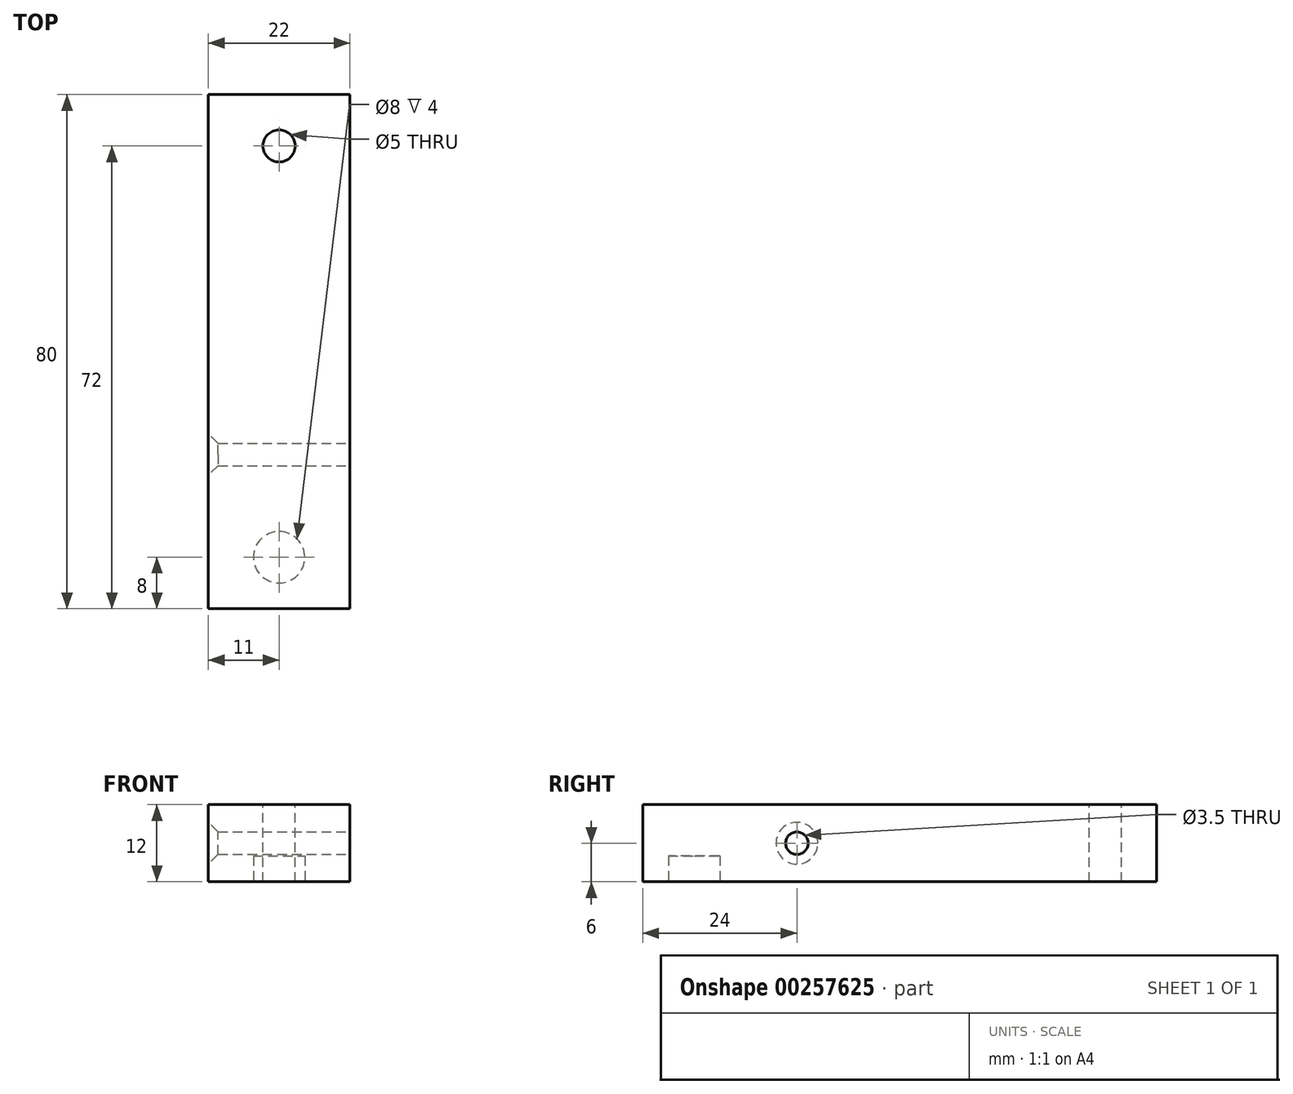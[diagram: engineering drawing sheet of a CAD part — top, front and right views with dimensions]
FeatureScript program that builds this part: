
annotation { "Feature Type Name" : "Feature", "Feature Type Description" : "" }
export const myFeature = defineFeature(function(context is Context, id is Id, definition is map)
    precondition{}
    {
        {
            var Q0;
            Q0=qCreatedBy(makeId("Top.planeOp"),FACE);
            var sketch = newSketch(context, id + "F0", { "sketchPlane" : qUnion([Q0])});
            skLineSegment(sketch, "E0.bottom", {"start": v(11, -40) * mm, "end": v(-11, -40) * mm});
            skLineSegment(sketch, "E0.top", {"start": v(11, 40) * mm, "end": v(-11, 40) * mm});
            skLineSegment(sketch, "E0.left", {"start": v(11, -40) * mm, "end": v(11, 40) * mm});
            skLineSegment(sketch, "E0.right", {"start": v(-11, -40) * mm, "end": v(-11, 40) * mm});
            skPoint(sketch, "E0.middle", {"position": v(0, 0) * mm});
            skSolve(sketch);
        }
        {
            var Q0;
            Q0 = qSketchRegion(id + "F0", true);
            extrude(context, id + "F1", {"entities" : qUnion([Q0]), "depth" : 12 * mm});
        }
        {
            var Q0;
            Q0=makeQuery(id+"F1.opExtrude","SWEPT_FACE",FACE,{"disambiguationData":[OSD([sQuery(id+"F0.wireOp",EDGE,"E0.left")])]});
            var sketch = newSketch(context, id + "F2", { "sketchPlane" : qUnion([Q0])});
            skCircle(sketch, "E1", {"center": v(-16, 6) * mm, "radius": 1.75 * mm});
            skSolve(sketch);
        }
        {
            var Q0;
            Q0 = qSketchRegion(id + "F2", true);
            extrude(context, id + "F3", {"entities" : qUnion([Q0]), "operationType" : NewBodyOperationType.REMOVE, "oppositeDirection" : true, "depth" : 25 * mm});
        }
        {
            var Q0;
            Q0=makeQuery(id+"F3.boolean.opBoolean","COPY",EDGE,{"derivedFrom":makeQuery(id+"F3.opExtrude","CAP_EDGE",EDGE,{"disambiguationData":[OSD([sQuery(id+"F2.wireOp",EDGE,"E1")])],"isStart":true})});
            var Q1;
            Q1=makeQuery(id+"F3.boolean.opBoolean","INTERSECT",EDGE,{"derivedFrom":[makeQuery(id+"F1.opExtrude","SWEPT_FACE",FACE,{"disambiguationData":[OSD([sQuery(id+"F0.wireOp",EDGE,"E0.right")])]}),makeQuery(id+"F3.opExtrude","SWEPT_FACE",FACE,{"disambiguationData":[OSD([sQuery(id+"F2.wireOp",EDGE,"E1")])]})]});
            chamfer(context, id + "F4", {"entities" : qUnion([Q0, Q1]), "width" : 1.5 * mm, "tangentPropagation" : true});
        }
        {
            var Q0;
            Q0=makeQuery(id+"F1.opExtrude","CAP_FACE",FACE,{"disambiguationData":[OSD([sQuery(id+"F0.wireOp",EDGE,"E0.bottom"),sQuery(id+"F0.wireOp",EDGE,"E0.top"),sQuery(id+"F0.wireOp",EDGE,"E0.left"),sQuery(id+"F0.wireOp",EDGE,"E0.right")])],"isStart":true});
            var sketch = newSketch(context, id + "F5", { "sketchPlane" : qUnion([Q0])});
            skCircle(sketch, "E2", {"center": v(0, 32) * mm, "radius": 4 * mm});
            skSolve(sketch);
        }
        {
            var Q0;
            Q0 = qSketchRegion(id + "F5", true);
            extrude(context, id + "F6", {"entities" : qUnion([Q0]), "operationType" : NewBodyOperationType.REMOVE, "oppositeDirection" : true, "depth" : 4 * mm});
        }
        {
            var Q0;
            Q0=makeQuery(id+"F1.opExtrude","CAP_FACE",FACE,{"disambiguationData":[OSD([sQuery(id+"F0.wireOp",EDGE,"E0.bottom"),sQuery(id+"F0.wireOp",EDGE,"E0.top"),sQuery(id+"F0.wireOp",EDGE,"E0.left"),sQuery(id+"F0.wireOp",EDGE,"E0.right")])],"isStart":false});
            var sketch = newSketch(context, id + "F7", { "sketchPlane" : qUnion([Q0])});
            skPoint(sketch, "E3", {"position": v(0, 32) * mm});
            skSolve(sketch);
        }
        {
            var Q0;
            Q0=sQuery(id+"F7.wireOp",VERTEX,"E3");
            var Q1;
            Q1=makeQuery(id+"F1.opExtrude","SWEPT_BODY",BODY,{"disambiguationData":[OSD([sQuery(id+"F0.wireOp",EDGE,"E0.bottom"),sQuery(id+"F0.wireOp",EDGE,"E0.top"),sQuery(id+"F0.wireOp",EDGE,"E0.left"),sQuery(id+"F0.wireOp",EDGE,"E0.right")])]});
            hole(context, id + "F8", {"style" : HoleStyle.SIMPLE, "endStyle" : HoleEndStyle.THROUGH, "standardTappedOrClearance" : lookupTablePath({ "standard" : "ISO", "engagement" : "75%", "pitch" : "1 mm", "size" : "M6", "type" : "Tapped" }), "standardBlindInLast" : lookupTablePath({ "standard" : "ISO", "engagement" : "75%", "pitch" : "1 mm", "size" : "M6", "type" : "Tapped" }), "holeDiameter" : 5 * mm, "showTappedDepth" : true, "tappedDepth" : 12 * mm, "tapClearance" : 3, "locations" : qUnion([Q0]), "scope" : qUnion([Q1]), "majorDiameter" : 6 * mm});
        }
    });
